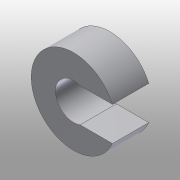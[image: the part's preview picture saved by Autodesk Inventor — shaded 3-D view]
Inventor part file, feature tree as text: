
AUTODESK INVENTOR PART (.ipt)
format: ipt  version: 2016 (Build 200138000, 138)  size: 89,088 bytes
history: native  units: mm
features: extrude x1, sketch x1
ambient origin geometry x8: Origin, YZ Plane, XZ Plane, XY Plane, X Axis, Y Axis, Z Axis, Center Point
bodies: Solid1 (feature_tree)
feature tree (2):
  extrude  "Extrusion1"  Depth=2.8mm
  sketch  "Sketch1"  dims[d0=7.0mm d1=2.8mm d2=1.5mm d3=3.0mm d4=0.0mm]
